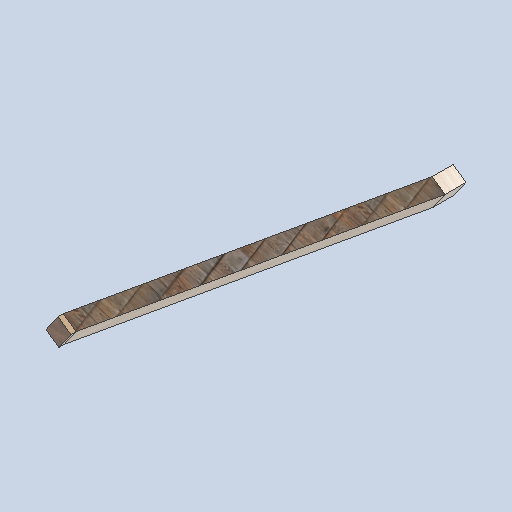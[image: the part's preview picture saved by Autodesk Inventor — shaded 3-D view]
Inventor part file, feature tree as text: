
AUTODESK INVENTOR PART (.ipt)
format: ipt  version: 2024.2 (Build 282272000, 272)  size: 136,192 bytes
history: native  units: in
note: dims shown in document units (in); Inventor stores cm internally (conversion verified against a paired STEP export)
features: sketch x4, other x3, plane x2
ambient origin geometry x8: Origin, YZ Plane, XZ Plane, XY Plane, X Axis, Y Axis, Z Axis, Center Point
bodies: Solid1 (feature_tree)
feature tree (9):
  other  "support_beam_segment_0102_MIR.ipt"
  other  "Solid1::support_beam_segment_0102_MIR.ipt"
  other  "TaggingFeature1"
  sketch  "Sketch1"  dims[d0=0.3937in]
  sketch  "Sketch2"
  sketch  "Sketch3"
  sketch  "Sketch4"
  plane  "Work Plane1"
  plane  "Work Plane2"
